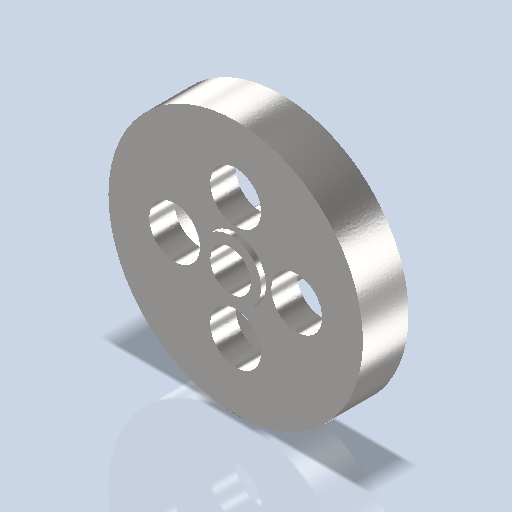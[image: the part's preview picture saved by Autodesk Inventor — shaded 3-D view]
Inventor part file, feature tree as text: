
AUTODESK INVENTOR PART (.ipt)
format: ipt  version: 2024 (Build 280153000, 153)  size: 193,024 bytes
history: native  units: mm
features: sketch x4, hole x2, revolve x1, extrude x1, pattern_circular x1
ambient origin geometry x8: Origin, YZ Plane, XZ Plane, XY Plane, X Axis, Y Axis, Z Axis, Center Point
bodies: Body1 (feature_tree)
feature tree (9):
  revolve  "Umdrehung1"
  extrude  "Extrusion3"  Depth=1.0mm
  hole  "Bohrung1"  [1 undecoded]
  hole  "Bohrung2"  [1 undecoded]
  pattern_circular  "Runde Anordnung1"  [2 undecoded]
  sketch  "Skizze4"  dims[d6=50.0mm d7=1.0mm]
  sketch  "Skizze5"  dims[d8=10.0mm d11=12.0mm]
  sketch  "Skizze6"  dims[d19=360.0deg d20=36.0mm]
  sketch  "Skizze7"  dims[d21=4.0mm d22=0.0mm d23=8.0mm d24=6.0mm d25=4.0mm d26=2.0mm d27=90.0deg d28=8.0mm d29=20.594885mm d31=24.0mm d32=10.0mm d33=6.0mm d34=4.0mm d35=2.0mm d36=90.0deg d37=8.0mm d38=20.594885mm d39=40.0mm d40=360.0deg]
note: 4 required parameter values undecoded (feature->parameter linkage not recoverable at this tier; creation-order binding heuristic only, values carry confidence <= 0.55)
